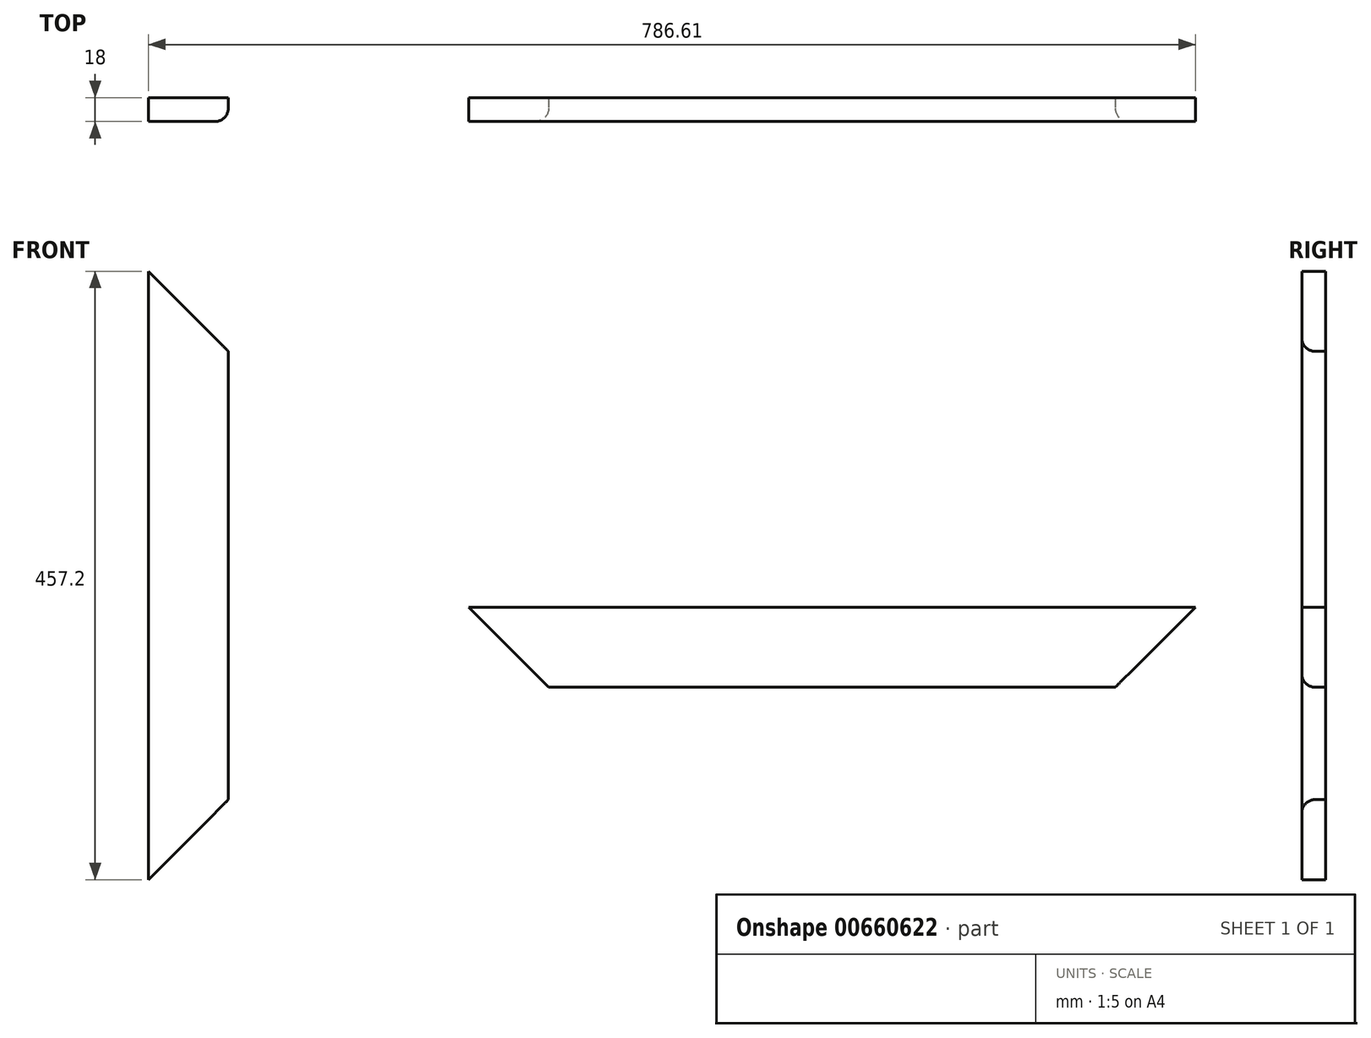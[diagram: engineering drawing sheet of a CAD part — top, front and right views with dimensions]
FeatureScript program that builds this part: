
annotation { "Feature Type Name" : "Feature", "Feature Type Description" : "" }
export const myFeature = defineFeature(function(context is Context, id is Id, definition is map)
    precondition{}
    {
        {
            var Q0;
            Q0=qCreatedBy(makeId("Front.planeOp"),FACE);
            var sketch = newSketch(context, id + "F0", { "sketchPlane" : qUnion([Q0])});
            skLineSegment(sketch, "E0.bottom", {"start": v(-252.1, -16.56) * mm, "end": v(294, -16.56) * mm});
            skLineSegment(sketch, "E0.top", {"start": v(-252.1, -76.56) * mm, "end": v(294, -76.56) * mm});
            skLineSegment(sketch, "E0.left", {"start": v(-252.1, -16.56) * mm, "end": v(-252.1, -76.56) * mm});
            skLineSegment(sketch, "E0.right", {"start": v(294, -16.56) * mm, "end": v(294, -76.56) * mm});
            skSolve(sketch);
        }
        {
            var Q0;
            Q0 = qSketchRegion(id + "F0", true);
            extrude(context, id + "F1", {"entities" : qUnion([Q0]), "depth" : 18 * mm, "offsetDistance" : 25 * mm});
        }
        {
            var Q0;
            Q0=makeQuery(id+"F1.opExtrude","CAP_FACE",FACE,{"disambiguationData":[OSD([sQuery(id+"F0.wireOp",EDGE,"E0.bottom"),sQuery(id+"F0.wireOp",EDGE,"E0.top"),sQuery(id+"F0.wireOp",EDGE,"E0.left"),sQuery(id+"F0.wireOp",EDGE,"E0.right")])],"isStart":false});
            var sketch = newSketch(context, id + "F2", { "sketchPlane" : qUnion([Q0])});
            skLineSegment(sketch, "E1", {"start": v(-252.1, -16.56) * mm, "end": v(-191.9, -76.56) * mm});
            skSolve(sketch);
        }
        {
            var Q0;
            {var subQ0=sQuery(id+"F2.wireOp",EDGE,"E1");Q0=makeQuery(id+"F2.imprint","IMPRINT",FACE,{"disambiguationData":[TD([[makeQuery(id+"F2.imprint","IMPRINT",EDGE,{"derivedFrom":subQ0}),-1.0]])]});}
            extrude(context, id + "F3", {"entities" : qUnion([Q0]), "operationType" : NewBodyOperationType.REMOVE, "endBound" : BoundingType.THROUGH_ALL, "oppositeDirection" : true, "depth" : 25 * mm, "offsetDistance" : 25 * mm});
        }
        {
            var Q0;
            Q0=makeQuery(id+"F1.opExtrude","CAP_FACE",FACE,{"disambiguationData":[OSD([sQuery(id+"F0.wireOp",EDGE,"E0.bottom"),sQuery(id+"F0.wireOp",EDGE,"E0.top"),sQuery(id+"F0.wireOp",EDGE,"E0.left"),sQuery(id+"F0.wireOp",EDGE,"E0.right")])],"isStart":false});
            var sketch = newSketch(context, id + "F4", { "sketchPlane" : qUnion([Q0])});
            skLineSegment(sketch, "E2", {"start": v(294, -16.56) * mm, "end": v(233.8, -76.56) * mm});
            skSolve(sketch);
        }
        {
            var Q0;
            {var subQ0=sQuery(id+"F4.wireOp",EDGE,"E2");Q0=makeQuery(id+"F4.imprint","IMPRINT",FACE,{"disambiguationData":[TD([[makeQuery(id+"F4.imprint","IMPRINT",EDGE,{"derivedFrom":subQ0}),1.0]])]});}
            extrude(context, id + "F5", {"entities" : qUnion([Q0]), "operationType" : NewBodyOperationType.REMOVE, "endBound" : BoundingType.THROUGH_ALL, "oppositeDirection" : true, "depth" : 25 * mm, "offsetDistance" : 25 * mm});
        }
        {
            var Q0;
            Q0=qCreatedBy(makeId("Front.planeOp"),FACE);
            var sketch = newSketch(context, id + "F6", { "sketchPlane" : qUnion([Q0])});
            skLineSegment(sketch, "E3.bottom", {"start": v(-492.61, 236.06) * mm, "end": v(-432.61, 236.06) * mm});
            skLineSegment(sketch, "E3.top", {"start": v(-492.61, -221.14) * mm, "end": v(-432.61, -221.14) * mm});
            skLineSegment(sketch, "E3.left", {"start": v(-492.61, 236.06) * mm, "end": v(-492.61, -221.14) * mm});
            skLineSegment(sketch, "E3.right", {"start": v(-432.61, 236.06) * mm, "end": v(-432.61, -221.14) * mm});
            skSolve(sketch);
        }
        {
            var Q0;
            Q0 = qSketchRegion(id + "F6", true);
            extrude(context, id + "F7", {"entities" : qUnion([Q0]), "depth" : 18 * mm, "offsetDistance" : 25 * mm});
        }
        {
            var Q0;
            Q0=makeQuery(id+"F7.opExtrude","CAP_FACE",FACE,{"disambiguationData":[OSD([sQuery(id+"F6.wireOp",EDGE,"E3.bottom"),sQuery(id+"F6.wireOp",EDGE,"E3.top"),sQuery(id+"F6.wireOp",EDGE,"E3.left"),sQuery(id+"F6.wireOp",EDGE,"E3.right")])],"isStart":false});
            var sketch = newSketch(context, id + "F8", { "sketchPlane" : qUnion([Q0])});
            skLineSegment(sketch, "E4", {"start": v(-492.61, 236.06) * mm, "end": v(-432.61, 175.85) * mm});
            skSolve(sketch);
        }
        {
            var Q0;
            {var subQ0=sQuery(id+"F8.wireOp",EDGE,"E4");Q0=makeQuery(id+"F8.imprint","IMPRINT",FACE,{"disambiguationData":[TD([[makeQuery(id+"F8.imprint","IMPRINT",EDGE,{"derivedFrom":subQ0}),1.0]])]});}
            extrude(context, id + "F9", {"entities" : qUnion([Q0]), "operationType" : NewBodyOperationType.REMOVE, "endBound" : BoundingType.THROUGH_ALL, "oppositeDirection" : true, "depth" : 25 * mm, "offsetDistance" : 25 * mm});
        }
        {
            var Q0;
            Q0=makeQuery(id+"F7.opExtrude","CAP_FACE",FACE,{"disambiguationData":[OSD([sQuery(id+"F6.wireOp",EDGE,"E3.bottom"),sQuery(id+"F6.wireOp",EDGE,"E3.top"),sQuery(id+"F6.wireOp",EDGE,"E3.left"),sQuery(id+"F6.wireOp",EDGE,"E3.right")])],"isStart":false});
            var sketch = newSketch(context, id + "F10", { "sketchPlane" : qUnion([Q0])});
            skLineSegment(sketch, "E5", {"start": v(-492.61, -221.14) * mm, "end": v(-432.61, -160.93) * mm});
            skSolve(sketch);
        }
        {
            var Q0;
            {var subQ0=sQuery(id+"F10.wireOp",EDGE,"E5");Q0=makeQuery(id+"F10.imprint","IMPRINT",FACE,{"disambiguationData":[TD([[makeQuery(id+"F10.imprint","IMPRINT",EDGE,{"derivedFrom":subQ0}),-1.0]])]});}
            extrude(context, id + "F11", {"entities" : qUnion([Q0]), "operationType" : NewBodyOperationType.REMOVE, "endBound" : BoundingType.THROUGH_ALL, "oppositeDirection" : true, "depth" : 25 * mm, "offsetDistance" : 25 * mm});
        }
        {
            var Q0;
            Q0=makeQuery(id+"F1.opExtrude","CAP_EDGE",EDGE,{"disambiguationData":[OSD([sQuery(id+"F0.wireOp",EDGE,"E0.top")])],"isStart":false});
            fillet(context, id + "F12", {"entities" : qUnion([Q0]), "radius" : 10 * mm, "tangentPropagation" : true, "allowEdgeOverflow" : false});
        }
        {
            var Q0;
            Q0=makeQuery(id+"F7.opExtrude","CAP_EDGE",EDGE,{"disambiguationData":[OSD([sQuery(id+"F6.wireOp",EDGE,"E3.right")])],"isStart":false});
            fillet(context, id + "F13", {"entities" : qUnion([Q0]), "radius" : 10 * mm, "tangentPropagation" : true, "allowEdgeOverflow" : false});
        }
    });
